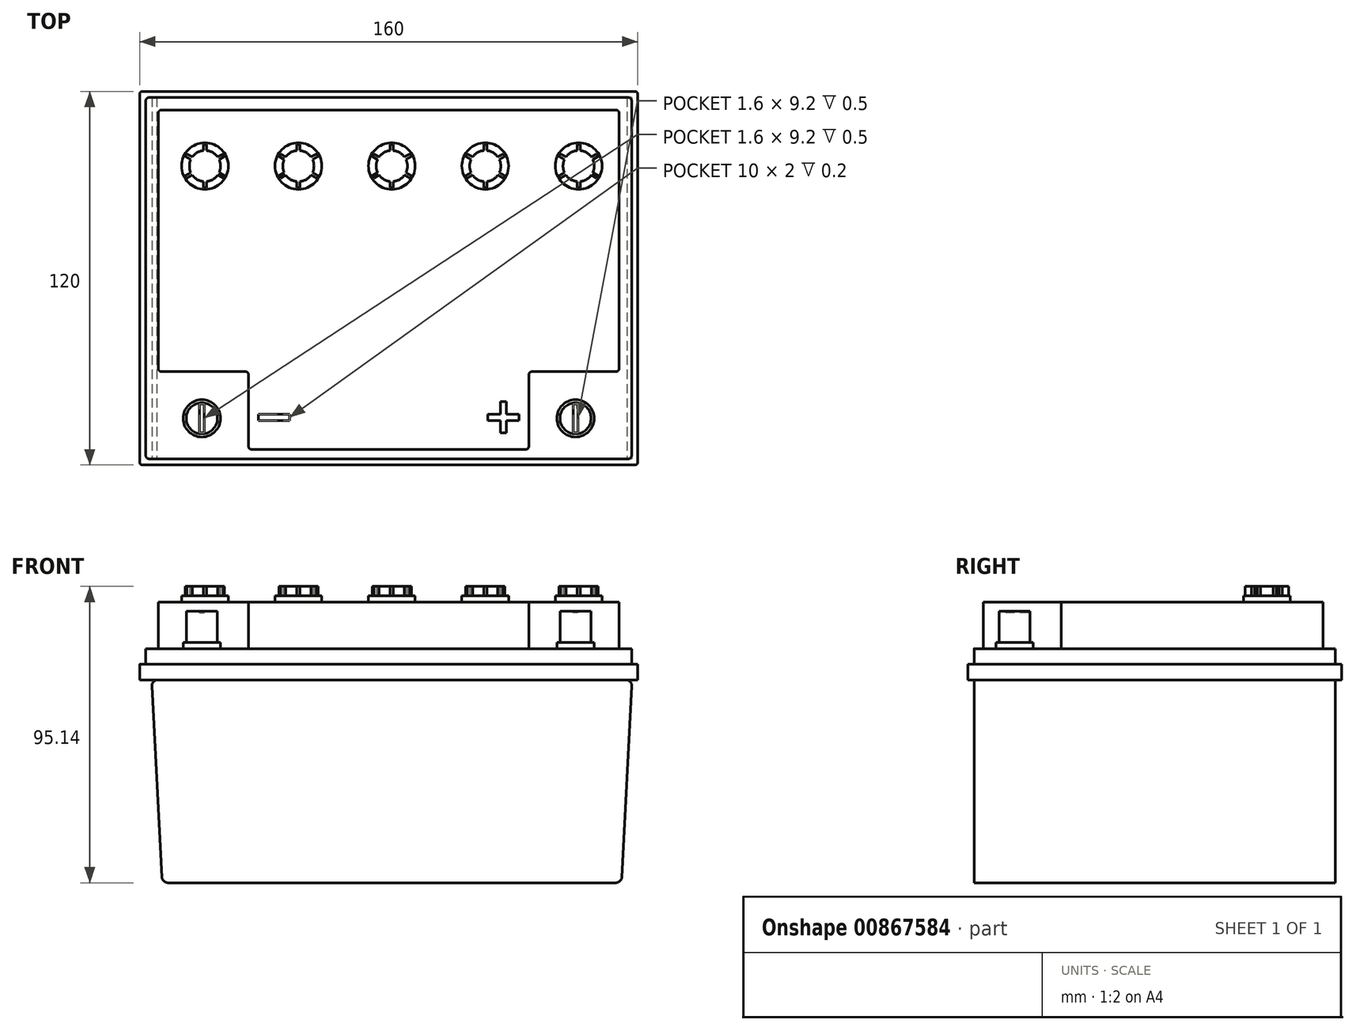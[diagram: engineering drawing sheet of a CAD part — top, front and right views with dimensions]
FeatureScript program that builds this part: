
annotation { "Feature Type Name" : "Feature", "Feature Type Description" : "" }
export const myFeature = defineFeature(function(context is Context, id is Id, definition is map)
    precondition{}
    {
        {
            var Q0;
            Q0=qCreatedBy(makeId("Top.planeOp"),FACE);
            var sketch = newSketch(context, id + "F0", { "sketchPlane" : qUnion([Q0])});
            skLineSegment(sketch, "E0", {"start": v(0, 57.54) * mm, "end": v(0, -70.76) * mm, "construction": true});
            skLineSegment(sketch, "E1", {"start": v(-66.1, 0) * mm, "end": v(85.26, 0) * mm, "construction": true});
            skLineSegment(sketch, "E2.bottom", {"start": v(-80, 60) * mm, "end": v(80, 60) * mm});
            skLineSegment(sketch, "E2.top", {"start": v(-80, -60) * mm, "end": v(80, -60) * mm});
            skLineSegment(sketch, "E2.left", {"start": v(-80, 60) * mm, "end": v(-80, -60) * mm});
            skLineSegment(sketch, "E2.right", {"start": v(80, 60) * mm, "end": v(80, -60) * mm});
            skSolve(sketch);
        }
        {
            var Q0;
            Q0=makeQuery(id+"F0.imprint","IMPRINT",FACE,{"disambiguationData":[TD([[makeQuery(id+"F0.imprint","IMPRINT",EDGE,{"derivedFrom":sQuery(id+"F0.wireOp",EDGE,"FddK9GHP-Q313-MpMC-0iAe-b5PYTbcDfMZE.bottom")}),1.0]])]});
            var Q1;
            Q1=makeQuery(id+"F0.imprint","IMPRINT",FACE,{"disambiguationData":[TD([[makeQuery(id+"F0.imprint","IMPRINT",EDGE,{"derivedFrom":sQuery(id+"F0.wireOp",EDGE,"E2.bottom")}),-1.0]])]});
            extrude(context, id + "F1", {"entities" : qUnion([Q0, Q1]), "depth" : 5 * mm, "offsetDistance" : 25.4 * mm});
        }
        {
            var Q0;
            Q0=makeQuery(id+"F1.opExtrude","CAP_FACE",FACE,{"disambiguationData":[OSD([sQuery(id+"F0.wireOp",EDGE,"E2.bottom"),sQuery(id+"F0.wireOp",EDGE,"E2.top"),sQuery(id+"F0.wireOp",EDGE,"E2.left"),sQuery(id+"F0.wireOp",EDGE,"E2.right")])],"isStart":false});
            var sketch = newSketch(context, id + "F2", { "sketchPlane" : qUnion([Q0])});
            skLineSegment(sketch, "E3.bottom", {"start": v(-78, 58) * mm, "end": v(78, 58) * mm});
            skLineSegment(sketch, "E3.top", {"start": v(-78, -58) * mm, "end": v(78, -58) * mm});
            skLineSegment(sketch, "E3.left", {"start": v(-78, 58) * mm, "end": v(-78, -58) * mm});
            skLineSegment(sketch, "E3.right", {"start": v(78, 58) * mm, "end": v(78, -58) * mm});
            skSolve(sketch);
        }
        {
            var Q0;
            Q0 = qSketchRegion(id + "F2", true);
            extrude(context, id + "F3", {"entities" : qUnion([Q0]), "operationType" : NewBodyOperationType.ADD, "depth" : 5 * mm, "offsetDistance" : 25 * mm});
        }
        {
            var Q0;
            Q0=makeQuery(id+"F3.opExtrude","CAP_FACE",FACE,{"disambiguationData":[OSD([sQuery(id+"F2.wireOp",EDGE,"E3.bottom"),sQuery(id+"F2.wireOp",EDGE,"E3.top"),sQuery(id+"F2.wireOp",EDGE,"E3.left"),sQuery(id+"F2.wireOp",EDGE,"E3.right")])],"isStart":false});
            var sketch = newSketch(context, id + "F4", { "sketchPlane" : qUnion([Q0])});
            skLineSegment(sketch, "E4.bottom", {"start": v(-74, 54) * mm, "end": v(74, 54) * mm});
            skLineSegment(sketch, "E4.left", {"start": v(-74, 54) * mm, "end": v(-74, -30) * mm});
            skLineSegment(sketch, "E4.right", {"start": v(74, 54) * mm, "end": v(74, -30) * mm});
            skLineSegment(sketch, "E5", {"start": v(-74, -30) * mm, "end": v(-45, -30) * mm});
            skLineSegment(sketch, "E6", {"start": v(-45, -30) * mm, "end": v(-45, -55) * mm});
            skLineSegment(sketch, "E7", {"start": v(-45, -55) * mm, "end": v(45, -55) * mm});
            skLineSegment(sketch, "E8", {"start": v(45, -55) * mm, "end": v(45, -30) * mm});
            skLineSegment(sketch, "E9", {"start": v(45, -30) * mm, "end": v(74, -30) * mm});
            skSolve(sketch);
        }
        {
            var Q0;
            Q0 = qSketchRegion(id + "F4", true);
            extrude(context, id + "F5", {"entities" : qUnion([Q0]), "operationType" : NewBodyOperationType.ADD, "depth" : 15 * mm, "offsetDistance" : 25 * mm});
        }
        {
            var Q0;
            Q0=makeQuery(id+"F3.opExtrude","CAP_FACE",FACE,{"disambiguationData":[OSD([sQuery(id+"F2.wireOp",EDGE,"E3.bottom"),sQuery(id+"F2.wireOp",EDGE,"E3.top"),sQuery(id+"F2.wireOp",EDGE,"E3.left"),sQuery(id+"F2.wireOp",EDGE,"E3.right")])],"isStart":false});
            var Q1;
            Q1=makeQuery(id+"F3.opExtrude","CAP_FACE",FACE,{"disambiguationData":[OSD([sQuery(id+"F2.wireOp",EDGE,"E3.bottom"),sQuery(id+"F2.wireOp",EDGE,"E3.top"),sQuery(id+"F2.wireOp",EDGE,"E3.left"),sQuery(id+"F2.wireOp",EDGE,"E3.right")])],"isStart":false});
            var sketch = newSketch(context, id + "F6", { "sketchPlane" : qUnion([Q0, Q1])});
            skCircle(sketch, "E10", {"center": v(-60, -45) * mm, "radius": 6 * mm});
            skCircle(sketch, "E11.MirrorC", {"center": v(60, -45) * mm, "radius": 6 * mm});
            skSolve(sketch);
        }
        {
            var Q0;
            Q0 = qSketchRegion(id + "F6", true);
            extrude(context, id + "F7", {"entities" : qUnion([Q0]), "operationType" : NewBodyOperationType.ADD, "depth" : 2 * mm, "offsetDistance" : 25 * mm});
        }
        {
            var Q0;
            Q0=makeQuery(id+"F7.opExtrude","CAP_FACE",FACE,{"disambiguationData":[OSD([sQuery(id+"F6.wireOp",EDGE,"E10")])],"isStart":false});
            var sketch = newSketch(context, id + "F8", { "sketchPlane" : qUnion([Q0])});
            skCircle(sketch, "E12", {"center": v(-60, -45) * mm, "radius": 5 * mm});
            skCircle(sketch, "E13.MirrorC", {"center": v(60, -45) * mm, "radius": 5 * mm});
            skSolve(sketch);
        }
        {
            var Q0;
            Q0 = qSketchRegion(id + "F8", true);
            extrude(context, id + "F9", {"entities" : qUnion([Q0]), "operationType" : NewBodyOperationType.ADD, "depth" : 10 * mm, "offsetDistance" : 25 * mm});
        }
        {
            var Q0;
            Q0=makeQuery(id+"F5.opExtrude","CAP_FACE",FACE,{"disambiguationData":[OSD([sQuery(id+"F4.wireOp",EDGE,"E4.bottom"),sQuery(id+"F4.wireOp",EDGE,"E4.left"),sQuery(id+"F4.wireOp",EDGE,"E4.right"),sQuery(id+"F4.wireOp",EDGE,"E5"),sQuery(id+"F4.wireOp",EDGE,"E6"),sQuery(id+"F4.wireOp",EDGE,"E7"),sQuery(id+"F4.wireOp",EDGE,"E8"),sQuery(id+"F4.wireOp",EDGE,"E9")])],"isStart":false});
            var sketch = newSketch(context, id + "F10", { "sketchPlane" : qUnion([Q0])});
            skLineSegment(sketch, "E14", {"start": v(-101.58, 36) * mm, "end": v(116.78, 36) * mm, "construction": true});
            skCircle(sketch, "E15", {"center": v(-59, 36) * mm, "radius": 7.5 * mm});
            skCircle(sketch, "E16.1.0.0", {"center": v(-29, 36) * mm, "radius": 7.5 * mm});
            skCircle(sketch, "E16.2.0.0", {"center": v(1, 36) * mm, "radius": 7.5 * mm});
            skCircle(sketch, "E16.3.0.0", {"center": v(31, 36) * mm, "radius": 7.5 * mm});
            skCircle(sketch, "E16.4.0.0", {"center": v(61, 36) * mm, "radius": 7.5 * mm});
            skLineSegment(sketch, "E16.direction1", {"start": v(-59, 36) * mm, "end": v(-29, 36) * mm, "construction": true});
            skSolve(sketch);
        }
        {
            var Q0;
            Q0 = qSketchRegion(id + "F10", true);
            extrude(context, id + "F11", {"entities" : qUnion([Q0]), "operationType" : NewBodyOperationType.ADD, "depth" : 2 * mm, "offsetDistance" : 25 * mm});
        }
        {
            var Q0;
            Q0=makeQuery(id+"F11.opExtrude","CAP_FACE",FACE,{"disambiguationData":[OSD([sQuery(id+"F10.wireOp",EDGE,"E15")])],"isStart":false});
            var sketch = newSketch(context, id + "F12", { "sketchPlane" : qUnion([Q0])});
            skArc(sketch, "E17", {"start": v(-63.56, 38.05) * mm, "mid": v(-64, 36) * mm, "end": v(-63.56, 33.95) * mm});
            skLineSegment(sketch, "E18", {"start": v(-59, 47.8) * mm, "end": v(-59, 18.52) * mm, "construction": true});
            skLineSegment(sketch, "E19", {"start": v(-59.5, 40.97) * mm, "end": v(-59.5, 42.97) * mm});
            skLineSegment(sketch, "E20", {"start": v(-59.5, 42.97) * mm, "end": v(-58.5, 42.97) * mm});
            skLineSegment(sketch, "E21", {"start": v(-58.5, 42.97) * mm, "end": v(-58.5, 40.97) * mm});
            skLineSegment(sketch, "E22.1.0", {"start": v(-64.8, 39.92) * mm, "end": v(-63.06, 38.92) * mm});
            skLineSegment(sketch, "E22.1.1", {"start": v(-63.56, 38.05) * mm, "end": v(-65.3, 39.05) * mm});
            skLineSegment(sketch, "E22.1.2", {"start": v(-65.3, 39.05) * mm, "end": v(-64.8, 39.92) * mm});
            skLineSegment(sketch, "E22.2.0", {"start": v(-65.3, 32.95) * mm, "end": v(-63.56, 33.95) * mm});
            skLineSegment(sketch, "E22.2.1", {"start": v(-63.06, 33.08) * mm, "end": v(-64.8, 32.08) * mm});
            skLineSegment(sketch, "E22.2.2", {"start": v(-64.8, 32.08) * mm, "end": v(-65.3, 32.95) * mm});
            skLineSegment(sketch, "E22.3.0", {"start": v(-59.5, 29.03) * mm, "end": v(-59.5, 31.03) * mm});
            skLineSegment(sketch, "E22.3.1", {"start": v(-58.5, 31.03) * mm, "end": v(-58.5, 29.03) * mm});
            skLineSegment(sketch, "E22.3.2", {"start": v(-58.5, 29.03) * mm, "end": v(-59.5, 29.03) * mm});
            skLineSegment(sketch, "E22.4.0", {"start": v(-53.2, 32.08) * mm, "end": v(-54.94, 33.08) * mm});
            skLineSegment(sketch, "E22.4.1", {"start": v(-54.44, 33.95) * mm, "end": v(-52.7, 32.95) * mm});
            skLineSegment(sketch, "E22.4.2", {"start": v(-52.7, 32.95) * mm, "end": v(-53.2, 32.08) * mm});
            skLineSegment(sketch, "E22.5.0", {"start": v(-52.7, 39.05) * mm, "end": v(-54.44, 38.05) * mm});
            skLineSegment(sketch, "E22.5.1", {"start": v(-54.94, 38.92) * mm, "end": v(-53.2, 39.92) * mm});
            skLineSegment(sketch, "E22.5.2", {"start": v(-53.2, 39.92) * mm, "end": v(-52.7, 39.05) * mm});
            skArc(sketch, "E23.trimOffspring", {"start": v(-59.5, 40.97) * mm, "mid": v(-61.5, 40.33) * mm, "end": v(-63.06, 38.92) * mm});
            skArc(sketch, "E24.trimOffspring", {"start": v(-54.94, 38.92) * mm, "mid": v(-56.5, 40.33) * mm, "end": v(-58.5, 40.97) * mm});
            skArc(sketch, "E25.trimOffspring", {"start": v(-63.06, 33.08) * mm, "mid": v(-61.5, 31.67) * mm, "end": v(-59.5, 31.03) * mm});
            skArc(sketch, "E26.trimOffspring", {"start": v(-54.44, 33.95) * mm, "mid": v(-54, 36) * mm, "end": v(-54.44, 38.05) * mm});
            skArc(sketch, "E27.trimOffspring", {"start": v(-58.5, 31.03) * mm, "mid": v(-56.5, 31.67) * mm, "end": v(-54.94, 33.08) * mm});
            skArc(sketch, "E28.1.0.0", {"start": v(-28.5, 31.03) * mm, "mid": v(-26.5, 31.67) * mm, "end": v(-24.94, 33.08) * mm});
            skLineSegment(sketch, "E28.1.0.1", {"start": v(-33.06, 33.08) * mm, "end": v(-34.8, 32.08) * mm});
            skLineSegment(sketch, "E28.1.0.2", {"start": v(-28.5, 31.03) * mm, "end": v(-28.5, 29.03) * mm});
            skArc(sketch, "E28.1.0.3", {"start": v(-29.5, 40.97) * mm, "mid": v(-31.5, 40.33) * mm, "end": v(-33.06, 38.92) * mm});
            skPoint(sketch, "E28.1.0.4", {"position": v(-29, 36) * mm});
            skLineSegment(sketch, "E28.1.0.5", {"start": v(-35.3, 32.95) * mm, "end": v(-33.56, 33.95) * mm});
            skLineSegment(sketch, "E28.1.0.6", {"start": v(-33.56, 38.05) * mm, "end": v(-35.3, 39.05) * mm});
            skLineSegment(sketch, "E28.1.0.7", {"start": v(-34.8, 39.92) * mm, "end": v(-33.06, 38.92) * mm});
            skLineSegment(sketch, "E28.1.0.8", {"start": v(-29.5, 29.03) * mm, "end": v(-29.5, 31.03) * mm});
            skArc(sketch, "E28.1.0.9", {"start": v(-33.06, 33.08) * mm, "mid": v(-31.5, 31.67) * mm, "end": v(-29.5, 31.03) * mm});
            skArc(sketch, "E28.1.0.10", {"start": v(-24.94, 38.92) * mm, "mid": v(-26.5, 40.33) * mm, "end": v(-28.5, 40.97) * mm});
            skArc(sketch, "E28.1.0.11", {"start": v(-24.44, 33.95) * mm, "mid": v(-24, 36) * mm, "end": v(-24.44, 38.05) * mm});
            skArc(sketch, "E28.1.0.12", {"start": v(-33.56, 38.05) * mm, "mid": v(-34, 36) * mm, "end": v(-33.56, 33.95) * mm});
            skLineSegment(sketch, "E28.1.0.13", {"start": v(-28.5, 42.97) * mm, "end": v(-28.5, 40.97) * mm});
            skLineSegment(sketch, "E28.1.0.14", {"start": v(-29.5, 40.97) * mm, "end": v(-29.5, 42.97) * mm});
            skLineSegment(sketch, "E28.1.0.15", {"start": v(-22.7, 32.95) * mm, "end": v(-23.2, 32.08) * mm});
            skLineSegment(sketch, "E28.1.0.16", {"start": v(-34.8, 32.08) * mm, "end": v(-35.3, 32.95) * mm});
            skLineSegment(sketch, "E28.1.0.17", {"start": v(-28.5, 29.03) * mm, "end": v(-29.5, 29.03) * mm});
            skLineSegment(sketch, "E28.1.0.18", {"start": v(-29.5, 42.97) * mm, "end": v(-28.5, 42.97) * mm});
            skLineSegment(sketch, "E28.1.0.19", {"start": v(-24.44, 33.95) * mm, "end": v(-22.7, 32.95) * mm});
            skLineSegment(sketch, "E28.1.0.20", {"start": v(-22.7, 39.05) * mm, "end": v(-24.44, 38.05) * mm});
            skLineSegment(sketch, "E28.1.0.21", {"start": v(-35.3, 39.05) * mm, "end": v(-34.8, 39.92) * mm});
            skLineSegment(sketch, "E28.1.0.22", {"start": v(-23.2, 32.08) * mm, "end": v(-24.94, 33.08) * mm});
            skLineSegment(sketch, "E28.1.0.23", {"start": v(-23.2, 39.92) * mm, "end": v(-22.7, 39.05) * mm});
            skLineSegment(sketch, "E28.1.0.24", {"start": v(-24.94, 38.92) * mm, "end": v(-23.2, 39.92) * mm});
            skArc(sketch, "E28.2.0.0", {"start": v(1.5, 31.03) * mm, "mid": v(3.5, 31.67) * mm, "end": v(5.06, 33.08) * mm});
            skLineSegment(sketch, "E28.2.0.1", {"start": v(-3.06, 33.08) * mm, "end": v(-4.8, 32.08) * mm});
            skLineSegment(sketch, "E28.2.0.2", {"start": v(1.5, 31.03) * mm, "end": v(1.5, 29.03) * mm});
            skArc(sketch, "E28.2.0.3", {"start": v(0.5, 40.97) * mm, "mid": v(-1.5, 40.33) * mm, "end": v(-3.06, 38.92) * mm});
            skPoint(sketch, "E28.2.0.4", {"position": v(1, 36) * mm});
            skLineSegment(sketch, "E28.2.0.5", {"start": v(-5.3, 32.95) * mm, "end": v(-3.56, 33.95) * mm});
            skLineSegment(sketch, "E28.2.0.6", {"start": v(-3.56, 38.05) * mm, "end": v(-5.3, 39.05) * mm});
            skLineSegment(sketch, "E28.2.0.7", {"start": v(-4.8, 39.92) * mm, "end": v(-3.06, 38.92) * mm});
            skLineSegment(sketch, "E28.2.0.8", {"start": v(0.5, 29.03) * mm, "end": v(0.5, 31.03) * mm});
            skArc(sketch, "E28.2.0.9", {"start": v(-3.06, 33.08) * mm, "mid": v(-1.5, 31.67) * mm, "end": v(0.5, 31.03) * mm});
            skArc(sketch, "E28.2.0.10", {"start": v(5.06, 38.92) * mm, "mid": v(3.5, 40.33) * mm, "end": v(1.5, 40.97) * mm});
            skArc(sketch, "E28.2.0.11", {"start": v(5.56, 33.95) * mm, "mid": v(6, 36) * mm, "end": v(5.56, 38.05) * mm});
            skArc(sketch, "E28.2.0.12", {"start": v(-3.56, 38.05) * mm, "mid": v(-4, 36) * mm, "end": v(-3.56, 33.95) * mm});
            skLineSegment(sketch, "E28.2.0.13", {"start": v(1.5, 42.97) * mm, "end": v(1.5, 40.97) * mm});
            skLineSegment(sketch, "E28.2.0.14", {"start": v(0.5, 40.97) * mm, "end": v(0.5, 42.97) * mm});
            skLineSegment(sketch, "E28.2.0.15", {"start": v(7.3, 32.95) * mm, "end": v(6.8, 32.08) * mm});
            skLineSegment(sketch, "E28.2.0.16", {"start": v(-4.8, 32.08) * mm, "end": v(-5.3, 32.95) * mm});
            skLineSegment(sketch, "E28.2.0.17", {"start": v(1.5, 29.03) * mm, "end": v(0.5, 29.03) * mm});
            skLineSegment(sketch, "E28.2.0.18", {"start": v(0.5, 42.97) * mm, "end": v(1.5, 42.97) * mm});
            skLineSegment(sketch, "E28.2.0.19", {"start": v(5.56, 33.95) * mm, "end": v(7.3, 32.95) * mm});
            skLineSegment(sketch, "E28.2.0.20", {"start": v(7.3, 39.05) * mm, "end": v(5.56, 38.05) * mm});
            skLineSegment(sketch, "E28.2.0.21", {"start": v(-5.3, 39.05) * mm, "end": v(-4.8, 39.92) * mm});
            skLineSegment(sketch, "E28.2.0.22", {"start": v(6.8, 32.08) * mm, "end": v(5.06, 33.08) * mm});
            skLineSegment(sketch, "E28.2.0.23", {"start": v(6.8, 39.92) * mm, "end": v(7.3, 39.05) * mm});
            skLineSegment(sketch, "E28.2.0.24", {"start": v(5.06, 38.92) * mm, "end": v(6.8, 39.92) * mm});
            skArc(sketch, "E28.3.0.0", {"start": v(31.5, 31.03) * mm, "mid": v(33.5, 31.67) * mm, "end": v(35.06, 33.08) * mm});
            skLineSegment(sketch, "E28.3.0.1", {"start": v(26.94, 33.08) * mm, "end": v(25.2, 32.08) * mm});
            skLineSegment(sketch, "E28.3.0.2", {"start": v(31.5, 31.03) * mm, "end": v(31.5, 29.03) * mm});
            skArc(sketch, "E28.3.0.3", {"start": v(30.5, 40.97) * mm, "mid": v(28.5, 40.33) * mm, "end": v(26.94, 38.92) * mm});
            skPoint(sketch, "E28.3.0.4", {"position": v(31, 36) * mm});
            skLineSegment(sketch, "E28.3.0.5", {"start": v(24.7, 32.95) * mm, "end": v(26.44, 33.95) * mm});
            skLineSegment(sketch, "E28.3.0.6", {"start": v(26.44, 38.05) * mm, "end": v(24.7, 39.05) * mm});
            skLineSegment(sketch, "E28.3.0.7", {"start": v(25.2, 39.92) * mm, "end": v(26.94, 38.92) * mm});
            skLineSegment(sketch, "E28.3.0.8", {"start": v(30.5, 29.03) * mm, "end": v(30.5, 31.03) * mm});
            skArc(sketch, "E28.3.0.9", {"start": v(26.94, 33.08) * mm, "mid": v(28.5, 31.67) * mm, "end": v(30.5, 31.03) * mm});
            skArc(sketch, "E28.3.0.10", {"start": v(35.06, 38.92) * mm, "mid": v(33.5, 40.33) * mm, "end": v(31.5, 40.97) * mm});
            skArc(sketch, "E28.3.0.11", {"start": v(35.56, 33.95) * mm, "mid": v(36, 36) * mm, "end": v(35.56, 38.05) * mm});
            skArc(sketch, "E28.3.0.12", {"start": v(26.44, 38.05) * mm, "mid": v(26, 36) * mm, "end": v(26.44, 33.95) * mm});
            skLineSegment(sketch, "E28.3.0.13", {"start": v(31.5, 42.97) * mm, "end": v(31.5, 40.97) * mm});
            skLineSegment(sketch, "E28.3.0.14", {"start": v(30.5, 40.97) * mm, "end": v(30.5, 42.97) * mm});
            skLineSegment(sketch, "E28.3.0.15", {"start": v(37.3, 32.95) * mm, "end": v(36.8, 32.08) * mm});
            skLineSegment(sketch, "E28.3.0.16", {"start": v(25.2, 32.08) * mm, "end": v(24.7, 32.95) * mm});
            skLineSegment(sketch, "E28.3.0.17", {"start": v(31.5, 29.03) * mm, "end": v(30.5, 29.03) * mm});
            skLineSegment(sketch, "E28.3.0.18", {"start": v(30.5, 42.97) * mm, "end": v(31.5, 42.97) * mm});
            skLineSegment(sketch, "E28.3.0.19", {"start": v(35.56, 33.95) * mm, "end": v(37.3, 32.95) * mm});
            skLineSegment(sketch, "E28.3.0.20", {"start": v(37.3, 39.05) * mm, "end": v(35.56, 38.05) * mm});
            skLineSegment(sketch, "E28.3.0.21", {"start": v(24.7, 39.05) * mm, "end": v(25.2, 39.92) * mm});
            skLineSegment(sketch, "E28.3.0.22", {"start": v(36.8, 32.08) * mm, "end": v(35.06, 33.08) * mm});
            skLineSegment(sketch, "E28.3.0.23", {"start": v(36.8, 39.92) * mm, "end": v(37.3, 39.05) * mm});
            skLineSegment(sketch, "E28.3.0.24", {"start": v(35.06, 38.92) * mm, "end": v(36.8, 39.92) * mm});
            skArc(sketch, "E28.4.0.0", {"start": v(61.5, 31.03) * mm, "mid": v(63.5, 31.67) * mm, "end": v(65.06, 33.08) * mm});
            skLineSegment(sketch, "E28.4.0.1", {"start": v(56.94, 33.08) * mm, "end": v(55.2, 32.08) * mm});
            skLineSegment(sketch, "E28.4.0.2", {"start": v(61.5, 31.03) * mm, "end": v(61.5, 29.03) * mm});
            skArc(sketch, "E28.4.0.3", {"start": v(60.5, 40.97) * mm, "mid": v(58.5, 40.33) * mm, "end": v(56.94, 38.92) * mm});
            skPoint(sketch, "E28.4.0.4", {"position": v(61, 36) * mm});
            skLineSegment(sketch, "E28.4.0.5", {"start": v(54.7, 32.95) * mm, "end": v(56.44, 33.95) * mm});
            skLineSegment(sketch, "E28.4.0.6", {"start": v(56.44, 38.05) * mm, "end": v(54.7, 39.05) * mm});
            skLineSegment(sketch, "E28.4.0.7", {"start": v(55.2, 39.92) * mm, "end": v(56.94, 38.92) * mm});
            skLineSegment(sketch, "E28.4.0.8", {"start": v(60.5, 29.03) * mm, "end": v(60.5, 31.03) * mm});
            skArc(sketch, "E28.4.0.9", {"start": v(56.94, 33.08) * mm, "mid": v(58.5, 31.67) * mm, "end": v(60.5, 31.03) * mm});
            skArc(sketch, "E28.4.0.10", {"start": v(65.06, 38.92) * mm, "mid": v(63.5, 40.33) * mm, "end": v(61.5, 40.97) * mm});
            skArc(sketch, "E28.4.0.11", {"start": v(65.56, 33.95) * mm, "mid": v(66, 36) * mm, "end": v(65.56, 38.05) * mm});
            skArc(sketch, "E28.4.0.12", {"start": v(56.44, 38.05) * mm, "mid": v(56, 36) * mm, "end": v(56.44, 33.95) * mm});
            skLineSegment(sketch, "E28.4.0.13", {"start": v(61.5, 42.97) * mm, "end": v(61.5, 40.97) * mm});
            skLineSegment(sketch, "E28.4.0.14", {"start": v(60.5, 40.97) * mm, "end": v(60.5, 42.97) * mm});
            skLineSegment(sketch, "E28.4.0.15", {"start": v(67.3, 32.95) * mm, "end": v(66.8, 32.08) * mm});
            skLineSegment(sketch, "E28.4.0.16", {"start": v(55.2, 32.08) * mm, "end": v(54.7, 32.95) * mm});
            skLineSegment(sketch, "E28.4.0.17", {"start": v(61.5, 29.03) * mm, "end": v(60.5, 29.03) * mm});
            skLineSegment(sketch, "E28.4.0.18", {"start": v(60.5, 42.97) * mm, "end": v(61.5, 42.97) * mm});
            skLineSegment(sketch, "E28.4.0.19", {"start": v(65.56, 33.95) * mm, "end": v(67.3, 32.95) * mm});
            skLineSegment(sketch, "E28.4.0.20", {"start": v(67.3, 39.05) * mm, "end": v(65.56, 38.05) * mm});
            skLineSegment(sketch, "E28.4.0.21", {"start": v(54.7, 39.05) * mm, "end": v(55.2, 39.92) * mm});
            skLineSegment(sketch, "E28.4.0.22", {"start": v(66.8, 32.08) * mm, "end": v(65.06, 33.08) * mm});
            skLineSegment(sketch, "E28.4.0.23", {"start": v(66.8, 39.92) * mm, "end": v(67.3, 39.05) * mm});
            skLineSegment(sketch, "E28.4.0.24", {"start": v(65.06, 38.92) * mm, "end": v(66.8, 39.92) * mm});
            skLineSegment(sketch, "E28.direction1", {"start": v(-64.8, 32.08) * mm, "end": v(-34.8, 32.08) * mm, "construction": true});
            skSolve(sketch);
        }
        {
            var Q0;
            Q0 = qSketchRegion(id + "F12", true);
            extrude(context, id + "F13", {"entities" : qUnion([Q0]), "operationType" : NewBodyOperationType.ADD, "depth" : 3 * mm, "offsetDistance" : 25 * mm});
        }
        {
            var Q0;
            Q0=makeQuery(id+"F9.opExtrude","CAP_FACE",FACE,{"disambiguationData":[OSD([sQuery(id+"F8.wireOp",EDGE,"E12")])],"isStart":false});
            var sketch = newSketch(context, id + "F14", { "sketchPlane" : qUnion([Q0])});
            skLineSegment(sketch, "E29.bottom", {"start": v(-60.8, -40.4) * mm, "end": v(-59.2, -40.4) * mm});
            skLineSegment(sketch, "E29.top", {"start": v(-60.8, -49.6) * mm, "end": v(-59.2, -49.6) * mm});
            skLineSegment(sketch, "E29.left", {"start": v(-60.8, -40.4) * mm, "end": v(-60.8, -49.6) * mm});
            skLineSegment(sketch, "E29.right", {"start": v(-59.2, -40.4) * mm, "end": v(-59.2, -49.6) * mm});
            skLineSegment(sketch, "E30.MirrorCS", {"start": v(59.2, -40.4) * mm, "end": v(59.2, -49.6) * mm});
            skLineSegment(sketch, "E31.MirrorCS", {"start": v(60.8, -49.6) * mm, "end": v(59.2, -49.6) * mm});
            skLineSegment(sketch, "E32.MirrorCS", {"start": v(60.8, -40.4) * mm, "end": v(59.2, -40.4) * mm});
            skLineSegment(sketch, "E33.MirrorCS", {"start": v(60.8, -40.4) * mm, "end": v(60.8, -49.6) * mm});
            skSolve(sketch);
        }
        {
            var Q0;
            Q0 = qSketchRegion(id + "F14", true);
            extrude(context, id + "F15", {"entities" : qUnion([Q0]), "operationType" : NewBodyOperationType.REMOVE, "oppositeDirection" : true, "depth" : 0.5 * mm, "offsetDistance" : 25 * mm});
        }
        {
            var Q0;
            Q0=makeQuery(id+"F5.opExtrude","SWEPT_EDGE",EDGE,{"disambiguationData":[OSD([sQuery(id+"F4.wireOp",EDGE,"E7"),sQuery(id+"F4.wireOp",EDGE,"E8")])]});
            var Q1;
            Q1=makeQuery(id+"F5.opExtrude","SWEPT_EDGE",EDGE,{"disambiguationData":[OSD([sQuery(id+"F4.wireOp",EDGE,"E4.right"),sQuery(id+"F4.wireOp",EDGE,"E9")])]});
            var Q2;
            Q2=makeQuery(id+"F5.opExtrude","SWEPT_EDGE",EDGE,{"disambiguationData":[OSD([sQuery(id+"F4.wireOp",EDGE,"E8"),sQuery(id+"F4.wireOp",EDGE,"E9")])]});
            var Q3;
            Q3=makeQuery(id+"F5.opExtrude","SWEPT_EDGE",EDGE,{"disambiguationData":[OSD([sQuery(id+"F4.wireOp",EDGE,"E6"),sQuery(id+"F4.wireOp",EDGE,"E7")])]});
            var Q4;
            Q4=makeQuery(id+"F5.opExtrude","SWEPT_EDGE",EDGE,{"disambiguationData":[OSD([sQuery(id+"F4.wireOp",EDGE,"E5"),sQuery(id+"F4.wireOp",EDGE,"E6")])]});
            var Q5;
            Q5=makeQuery(id+"F5.opExtrude","SWEPT_EDGE",EDGE,{"disambiguationData":[OSD([sQuery(id+"F4.wireOp",EDGE,"E4.left"),sQuery(id+"F4.wireOp",EDGE,"E5")])]});
            var Q6;
            Q6=makeQuery(id+"F5.opExtrude","SWEPT_EDGE",EDGE,{"disambiguationData":[OSD([sQuery(id+"F4.wireOp",EDGE,"E4.bottom"),sQuery(id+"F4.wireOp",EDGE,"E4.left")])]});
            var Q7;
            Q7=makeQuery(id+"F5.opExtrude","SWEPT_EDGE",EDGE,{"disambiguationData":[OSD([sQuery(id+"F4.wireOp",EDGE,"E4.bottom"),sQuery(id+"F4.wireOp",EDGE,"E4.right")])]});
            var Q8;
            Q8=makeQuery(id+"F3.opExtrude","SWEPT_EDGE",EDGE,{"disambiguationData":[OSD([sQuery(id+"F2.wireOp",EDGE,"E3.top"),sQuery(id+"F2.wireOp",EDGE,"E3.right")])]});
            var Q9;
            Q9=makeQuery(id+"F1.opExtrude","SWEPT_EDGE",EDGE,{"disambiguationData":[OSD([sQuery(id+"F0.wireOp",EDGE,"E2.top"),sQuery(id+"F0.wireOp",EDGE,"E2.right")])]});
            var Q10;
            Q10=makeQuery(id+"F3.opExtrude","SWEPT_EDGE",EDGE,{"disambiguationData":[OSD([sQuery(id+"F2.wireOp",EDGE,"E3.bottom"),sQuery(id+"F2.wireOp",EDGE,"E3.right")])]});
            var Q11;
            Q11=makeQuery(id+"F1.opExtrude","SWEPT_EDGE",EDGE,{"disambiguationData":[OSD([sQuery(id+"F0.wireOp",EDGE,"E2.bottom"),sQuery(id+"F0.wireOp",EDGE,"E2.right")])]});
            var Q12;
            Q12=makeQuery(id+"F3.opExtrude","SWEPT_EDGE",EDGE,{"disambiguationData":[OSD([sQuery(id+"F2.wireOp",EDGE,"E3.top"),sQuery(id+"F2.wireOp",EDGE,"E3.left")])]});
            var Q13;
            Q13=makeQuery(id+"F1.opExtrude","SWEPT_EDGE",EDGE,{"disambiguationData":[OSD([sQuery(id+"F0.wireOp",EDGE,"E2.top"),sQuery(id+"F0.wireOp",EDGE,"E2.left")])]});
            var Q14;
            Q14=makeQuery(id+"F3.opExtrude","SWEPT_EDGE",EDGE,{"disambiguationData":[OSD([sQuery(id+"F2.wireOp",EDGE,"E3.bottom"),sQuery(id+"F2.wireOp",EDGE,"E3.left")])]});
            var Q15;
            Q15=makeQuery(id+"F1.opExtrude","SWEPT_EDGE",EDGE,{"disambiguationData":[OSD([sQuery(id+"F0.wireOp",EDGE,"E2.bottom"),sQuery(id+"F0.wireOp",EDGE,"E2.left")])]});
            fillet(context, id + "F16", {"entities" : qUnion([Q0, Q1, Q2, Q3, Q4, Q5, Q6, Q7, Q8, Q9, Q10, Q11, Q12, Q13, Q14, Q15]), "radius" : 1 * mm, "tangentPropagation" : true, "allowEdgeOverflow" : false});
        }
        {
            var Q0;
            Q0=makeQuery(id+"F5.opExtrude","CAP_FACE",FACE,{"disambiguationData":[OSD([sQuery(id+"F4.wireOp",EDGE,"E4.bottom"),sQuery(id+"F4.wireOp",EDGE,"E4.left"),sQuery(id+"F4.wireOp",EDGE,"E4.right"),sQuery(id+"F4.wireOp",EDGE,"E5"),sQuery(id+"F4.wireOp",EDGE,"E6"),sQuery(id+"F4.wireOp",EDGE,"E7"),sQuery(id+"F4.wireOp",EDGE,"E8"),sQuery(id+"F4.wireOp",EDGE,"E9")])],"isStart":false});
            var sketch = newSketch(context, id + "F17", { "sketchPlane" : qUnion([Q0])});
            skLineSegment(sketch, "E34", {"start": v(36.84, -58.53) * mm, "end": v(36.84, -30.82) * mm, "construction": true});
            skPoint(sketch, "E34.startSnap0", {"position": v(36.84, -30.82) * mm});
            skLineSegment(sketch, "E35", {"start": v(-45.1, -44.67) * mm, "end": v(-27.43, -44.67) * mm});
            skPoint(sketch, "E35.startSnap0", {"position": v(36.84, -44.67) * mm});
            skLineSegment(sketch, "E36.bottom", {"start": v(31.84, -43.67) * mm, "end": v(35.84, -43.67) * mm});
            skLineSegment(sketch, "E36.top", {"start": v(31.84, -45.67) * mm, "end": v(35.84, -45.67) * mm});
            skLineSegment(sketch, "E36.left", {"start": v(31.84, -43.67) * mm, "end": v(31.84, -45.67) * mm});
            skLineSegment(sketch, "E36.right", {"start": v(41.84, -43.67) * mm, "end": v(41.84, -45.67) * mm});
            skLineSegment(sketch, "E37.bottom", {"start": v(35.84, -39.67) * mm, "end": v(37.84, -39.67) * mm});
            skLineSegment(sketch, "E37.top", {"start": v(35.84, -49.67) * mm, "end": v(37.84, -49.67) * mm});
            skLineSegment(sketch, "E37.left", {"start": v(35.84, -39.67) * mm, "end": v(35.84, -43.67) * mm});
            skLineSegment(sketch, "E37.right", {"start": v(37.84, -39.67) * mm, "end": v(37.84, -43.67) * mm});
            skLineSegment(sketch, "E38.MirrorCS", {"start": v(-41.84, -43.67) * mm, "end": v(-41.84, -45.67) * mm});
            skLineSegment(sketch, "E39.MirrorCS", {"start": v(-31.84, -43.67) * mm, "end": v(-31.84, -45.67) * mm});
            skLineSegment(sketch, "E40.MirrorCS", {"start": v(-31.84, -43.67) * mm, "end": v(-41.84, -43.67) * mm});
            skLineSegment(sketch, "E41.MirrorCS", {"start": v(-31.84, -45.67) * mm, "end": v(-41.84, -45.67) * mm});
            skLineSegment(sketch, "E42.trimOffspring", {"start": v(37.84, -43.67) * mm, "end": v(41.84, -43.67) * mm});
            skLineSegment(sketch, "E43.trimOffspring", {"start": v(35.84, -45.67) * mm, "end": v(35.84, -49.67) * mm});
            skLineSegment(sketch, "E44.trimOffspring", {"start": v(37.84, -45.67) * mm, "end": v(41.84, -45.67) * mm});
            skLineSegment(sketch, "E45.trimOffspring", {"start": v(37.84, -45.67) * mm, "end": v(37.84, -49.67) * mm});
            skSolve(sketch);
        }
        {
            var Q0;
            Q0 = qSketchRegion(id + "F17", true);
            extrude(context, id + "F18", {"entities" : qUnion([Q0]), "operationType" : NewBodyOperationType.REMOVE, "oppositeDirection" : true, "depth" : 0.2 * mm, "offsetDistance" : 25 * mm});
        }
        {
            var Q0;
            Q0=makeQuery(id+"F3.opExtrude","SWEPT_FACE",FACE,{"disambiguationData":[OSD([sQuery(id+"F2.wireOp",EDGE,"E3.top")])]});
            var sketch = newSketch(context, id + "F19", { "sketchPlane" : qUnion([Q0])});
            skLineSegment(sketch, "E46.bottom", {"start": v(-74.05, 0.04) * mm, "end": v(76.08, 0.04) * mm});
            skLineSegment(sketch, "E46.top", {"start": v(-70.84, -65.14) * mm, "end": v(72.88, -65.14) * mm});
            skLineSegment(sketch, "E47", {"start": v(-76.04, -2.07) * mm, "end": v(-72.84, -63.24) * mm});
            skLineSegment(sketch, "E48.MirrorCS", {"start": v(78.08, -2.07) * mm, "end": v(74.87, -63.24) * mm});
            skPoint(sketch, "E49.visualSharp", {"position": v(-72.74, -65.14) * mm});
            skArc(sketch, "E49.filletArc", {"start": v(-72.84, -63.24) * mm, "mid": v(-72.22, -64.6) * mm, "end": v(-70.84, -65.14) * mm});
            skPoint(sketch, "E50.visualSharp", {"position": v(74.78, -65.14) * mm});
            skArc(sketch, "E50.filletArc", {"start": v(72.88, -65.14) * mm, "mid": v(74.25, -64.6) * mm, "end": v(74.87, -63.24) * mm});
            skPoint(sketch, "E51.visualSharp", {"position": v(-76.15, 0.04) * mm});
            skArc(sketch, "E51.filletArc", {"start": v(-74.05, 0.04) * mm, "mid": v(-75.5, -0.59) * mm, "end": v(-76.04, -2.07) * mm});
            skPoint(sketch, "E52.visualSharp", {"position": v(78.2, 0.04) * mm});
            skArc(sketch, "E52.filletArc", {"start": v(78.08, -2.07) * mm, "mid": v(77.53, -0.59) * mm, "end": v(76.08, 0.04) * mm});
            skLineSegment(sketch, "E53", {"start": v(1.02, -87.12) * mm, "end": v(1.02, 65.42) * mm, "construction": true});
            skPoint(sketch, "E53.startSnap0", {"position": v(1.02, -65.14) * mm});
            skSolve(sketch);
        }
        {
            var Q0;
            Q0 = qSketchRegion(id + "F19", true);
            extrude(context, id + "F20", {"entities" : qUnion([Q0]), "operationType" : NewBodyOperationType.ADD, "oppositeDirection" : true, "depth" : 116 * mm, "offsetDistance" : 25 * mm});
        }
    });
